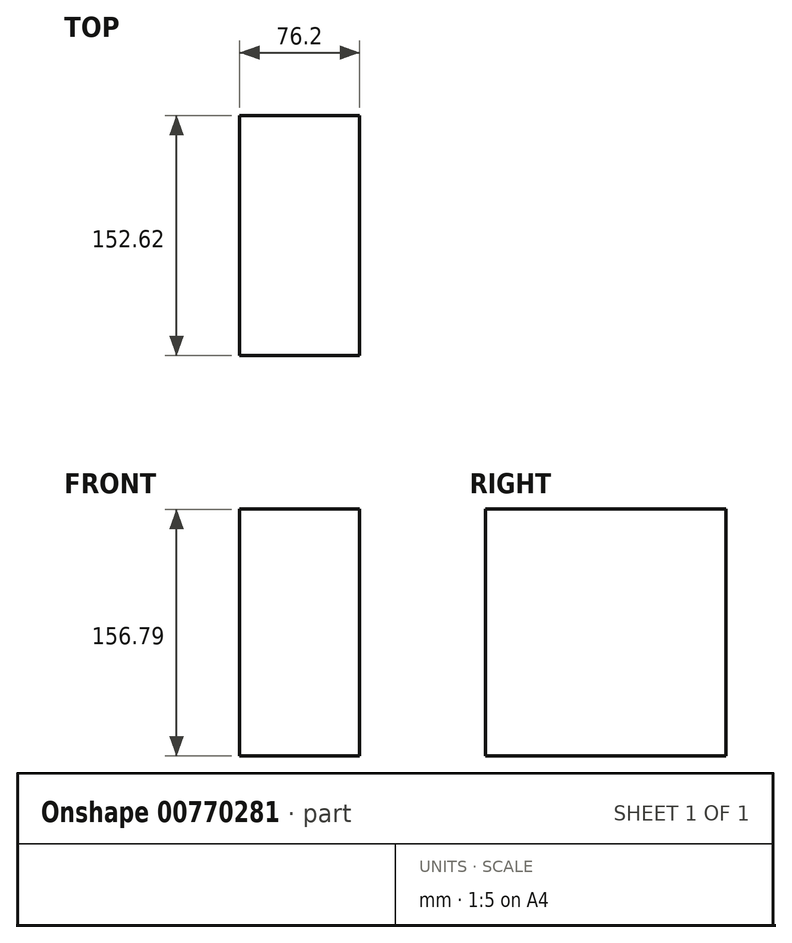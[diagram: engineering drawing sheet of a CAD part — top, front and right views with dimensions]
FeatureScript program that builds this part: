
annotation { "Feature Type Name" : "Feature", "Feature Type Description" : "" }
export const myFeature = defineFeature(function(context is Context, id is Id, definition is map)
    precondition{}
    {
        {
            var Q0;
            Q0=qCreatedBy(makeId("Right.planeOp"),FACE);
            var sketch = newSketch(context, id + "F0", { "sketchPlane" : qUnion([Q0])});
            skLineSegment(sketch, "E0.bottom", {"start": v(-76.31, 75.74) * mm, "end": v(76.31, 75.74) * mm});
            skLineSegment(sketch, "E0.top", {"start": v(-76.31, -55.65) * mm, "end": v(76.31, -55.65) * mm});
            skLineSegment(sketch, "E0.left", {"start": v(-76.31, 75.74) * mm, "end": v(-76.31, -55.65) * mm});
            skLineSegment(sketch, "E0.right", {"start": v(76.31, 75.74) * mm, "end": v(76.31, -55.65) * mm});
            skSolve(sketch);
        }
        {
            var Q0;
            Q0 = qSketchRegion(id + "F0", true);
            extrude(context, id + "F1", {"entities" : qUnion([Q0]), "depth" : 76.2 * mm, "offsetDistance" : 25.4 * mm});
        }
        {
            var Q0;
            Q0=makeQuery(id+"F1.opExtrude","SWEPT_FACE",FACE,{"disambiguationData":[OSD([sQuery(id+"F0.wireOp",EDGE,"E0.top")])]});
            extrude(context, id + "F2", {"entities" : qUnion([Q0]), "operationType" : NewBodyOperationType.ADD, "depth" : 25.4 * mm, "offsetDistance" : 25.4 * mm});
        }
    });
